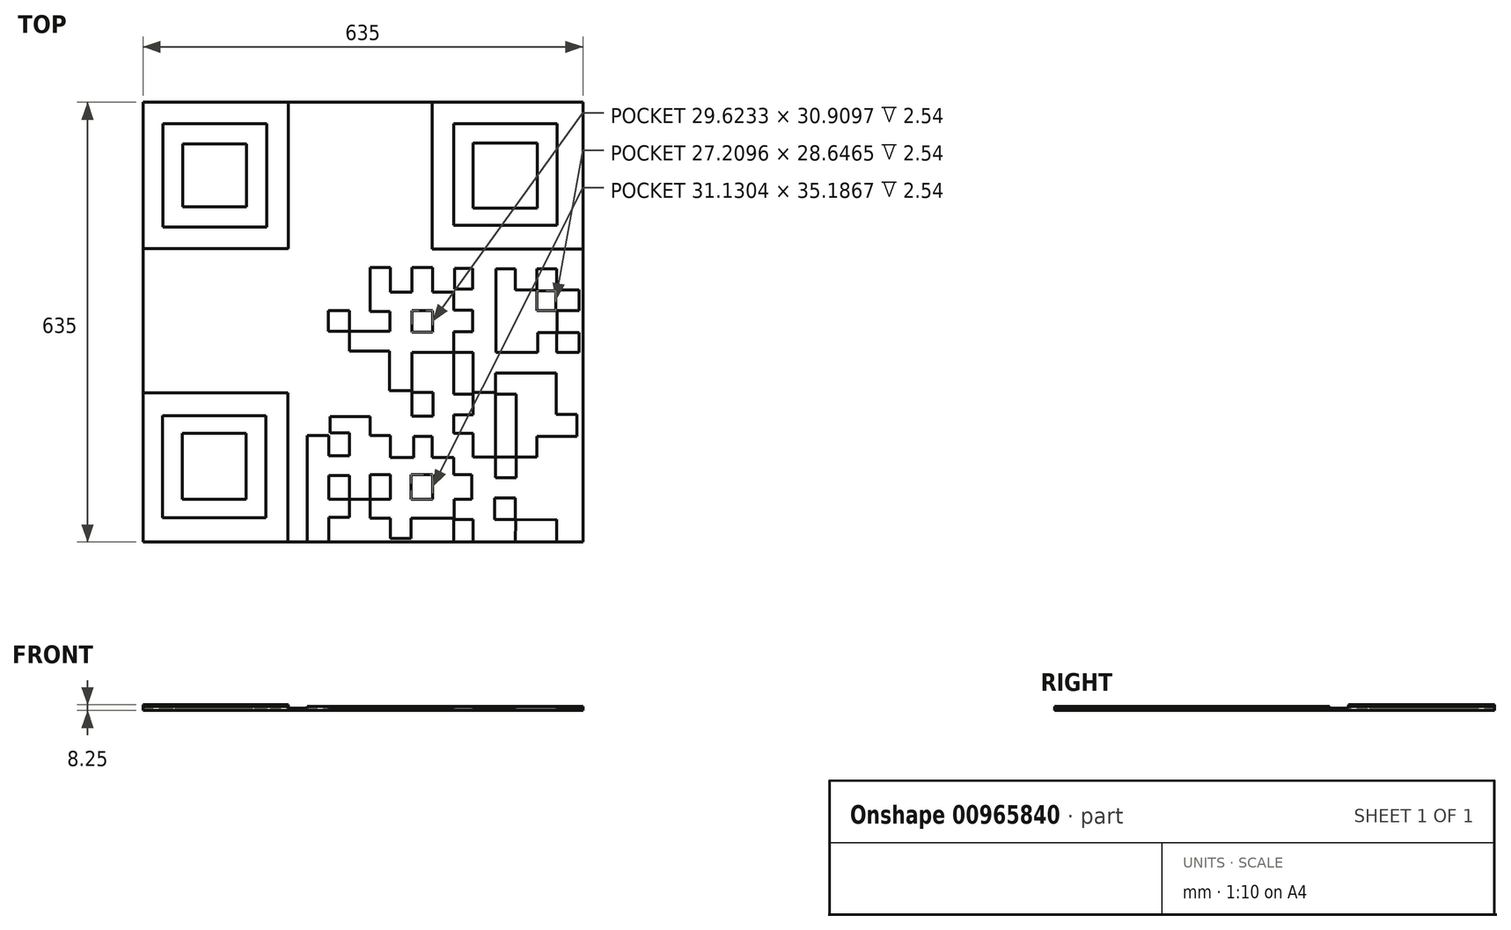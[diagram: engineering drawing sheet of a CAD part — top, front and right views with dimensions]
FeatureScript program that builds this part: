
annotation { "Feature Type Name" : "Feature", "Feature Type Description" : "" }
export const myFeature = defineFeature(function(context is Context, id is Id, definition is map)
    precondition{}
    {
        {
            var Q0;
            Q0=qCreatedBy(makeId("Top.planeOp"),FACE);
            var sketch = newSketch(context, id + "F0", { "sketchPlane" : qUnion([Q0])});
            skLineSegment(sketch, "E0.bottom", {"start": v(-317.5, 317.5) * mm, "end": v(317.5, 317.5) * mm});
            skLineSegment(sketch, "E0.top", {"start": v(-317.5, -317.5) * mm, "end": v(317.5, -317.5) * mm});
            skLineSegment(sketch, "E0.left", {"start": v(-317.5, 317.5) * mm, "end": v(-317.5, -317.5) * mm});
            skLineSegment(sketch, "E0.right", {"start": v(317.5, 317.5) * mm, "end": v(317.5, -317.5) * mm});
            skPoint(sketch, "E0.middle", {"position": v(0, 0) * mm});
            skSolve(sketch);
        }
        {
            var Q0;
            Q0=makeQuery(id+"F0.imprint","IMPRINT",FACE,{"disambiguationData":[TD([[makeQuery(id+"F0.imprint","IMPRINT",EDGE,{"derivedFrom":sQuery(id+"F0.wireOp",EDGE,"E0.bottom")}),-1.0]])]});
            extrude(context, id + "F1", {"entities" : qUnion([Q0]), "oppositeDirection" : true, "depth" : 3.17 * mm, "offsetDistance" : 25.4 * mm});
        }
        {
            var Q0;
            Q0=makeQuery(id+"F1.opExtrude","CAP_FACE",FACE,{"disambiguationData":[OSD([sQuery(id+"F0.wireOp",EDGE,"E0.bottom"),sQuery(id+"F0.wireOp",EDGE,"E0.top"),sQuery(id+"F0.wireOp",EDGE,"E0.left"),sQuery(id+"F0.wireOp",EDGE,"E0.right")])],"isStart":true});
            var sketch = newSketch(context, id + "F2", { "sketchPlane" : qUnion([Q0])});
            skLineSegment(sketch, "E1.bottom", {"start": v(-317.5, 317.5) * mm, "end": v(-107.8, 317.5) * mm});
            skLineSegment(sketch, "E1.top", {"start": v(-317.5, 106.2) * mm, "end": v(-107.8, 106.2) * mm});
            skLineSegment(sketch, "E1.left", {"start": v(-317.5, 317.5) * mm, "end": v(-317.5, 106.2) * mm});
            skLineSegment(sketch, "E1.right", {"start": v(-107.8, 317.5) * mm, "end": v(-107.8, 106.2) * mm});
            skLineSegment(sketch, "E2.bottom", {"start": v(-288.97, 286.94) * mm, "end": v(-139.14, 286.94) * mm});
            skLineSegment(sketch, "E2.top", {"start": v(-288.97, 137.11) * mm, "end": v(-139.14, 137.11) * mm});
            skLineSegment(sketch, "E2.left", {"start": v(-288.97, 286.94) * mm, "end": v(-288.97, 137.11) * mm});
            skLineSegment(sketch, "E2.right", {"start": v(-139.14, 286.94) * mm, "end": v(-139.14, 137.11) * mm});
            skLineSegment(sketch, "E3.bottom", {"start": v(-168.34, 166.3) * mm, "end": v(-260.2, 166.3) * mm});
            skLineSegment(sketch, "E3.top", {"start": v(-168.34, 257.32) * mm, "end": v(-260.2, 257.32) * mm});
            skLineSegment(sketch, "E3.left", {"start": v(-168.34, 166.3) * mm, "end": v(-168.34, 257.32) * mm});
            skLineSegment(sketch, "E3.right", {"start": v(-260.2, 166.3) * mm, "end": v(-260.2, 257.32) * mm});
            skLineSegment(sketch, "E4.bottom", {"start": v(-78.87, 287.97) * mm, "end": v(-18.76, 287.97) * mm});
            skLineSegment(sketch, "E4.top", {"start": v(-78.87, 257.32) * mm, "end": v(-19.2, 257.32) * mm});
            skLineSegment(sketch, "E4.left", {"start": v(-78.87, 287.97) * mm, "end": v(-78.87, 257.32) * mm});
            skLineSegment(sketch, "E4.right", {"start": v(8.71, 287.97) * mm, "end": v(8.71, 257.32) * mm});
            skLineSegment(sketch, "E5.bottom", {"start": v(8.71, 257.32) * mm, "end": v(40.9, 257.32) * mm});
            skLineSegment(sketch, "E5.top", {"start": v(-18.99, 226.58) * mm, "end": v(40.9, 226.58) * mm});
            skLineSegment(sketch, "E5.left", {"start": v(-19.2, 257.32) * mm, "end": v(-19.2, 226.58) * mm});
            skLineSegment(sketch, "E5.right", {"start": v(69.67, 257.32) * mm, "end": v(69.67, 226.58) * mm});
            skLineSegment(sketch, "E6.bottom", {"start": v(69.67, 167.76) * mm, "end": v(41.78, 167.76) * mm});
            skLineSegment(sketch, "E6.top", {"start": v(69.67, 312.44) * mm, "end": v(40.9, 312.44) * mm});
            skLineSegment(sketch, "E6.left", {"start": v(69.67, 167.76) * mm, "end": v(69.67, 312.44) * mm});
            skLineSegment(sketch, "E6.right", {"start": v(40.9, 167.76) * mm, "end": v(40.9, 226.58) * mm});
            skLineSegment(sketch, "E7.bottom", {"start": v(40.9, 312.44) * mm, "end": v(-18.76, 312.44) * mm});
            skLineSegment(sketch, "E7.top", {"start": v(40.9, 287.97) * mm, "end": v(8.71, 287.97) * mm});
            skLineSegment(sketch, "E7.right", {"start": v(-18.76, 312.44) * mm, "end": v(-18.76, 287.97) * mm});
            skLineSegment(sketch, "E8.trimOffspring", {"start": v(40.9, 257.32) * mm, "end": v(40.9, 287.97) * mm});
            skLineSegment(sketch, "E9.bottom", {"start": v(-19.2, 226.58) * mm, "end": v(-81.01, 226.58) * mm});
            skLineSegment(sketch, "E9.top", {"start": v(-19.2, 165.19) * mm, "end": v(-49.61, 165.19) * mm});
            skLineSegment(sketch, "E9.left", {"start": v(-19.2, 226.24) * mm, "end": v(-19.2, 165.19) * mm});
            skLineSegment(sketch, "E9.right", {"start": v(-81.01, 226.58) * mm, "end": v(-81.01, 197.82) * mm});
            skLineSegment(sketch, "E10.top", {"start": v(-81.01, 197.82) * mm, "end": v(-49.67, 197.82) * mm});
            skLineSegment(sketch, "E10.right", {"start": v(-49.67, 165.19) * mm, "end": v(-49.67, 197.82) * mm});
            skLineSegment(sketch, "E11.bottom", {"start": v(-49.67, 165.19) * mm, "end": v(-81.44, 165.19) * mm});
            skLineSegment(sketch, "E11.top", {"start": v(-49.67, 106.8) * mm, "end": v(-81.44, 106.8) * mm});
            skLineSegment(sketch, "E11.left", {"start": v(-49.67, 165.14) * mm, "end": v(-49.67, 106.83) * mm});
            skLineSegment(sketch, "E11.right", {"start": v(-81.44, 165.19) * mm, "end": v(-81.44, 106.8) * mm});
            skLineSegment(sketch, "E12.bottom", {"start": v(-49.66, 106.8) * mm, "end": v(-19.2, 106.8) * mm});
            skLineSegment(sketch, "E12.top", {"start": v(-49.6, 77.61) * mm, "end": v(-19.2, 77.61) * mm});
            skLineSegment(sketch, "E12.left", {"start": v(-49.67, 106.8) * mm, "end": v(-49.67, 77.61) * mm});
            skLineSegment(sketch, "E12.right", {"start": v(-19.2, 106.73) * mm, "end": v(-19.2, 77.61) * mm});
            skLineSegment(sketch, "E13.bottom", {"start": v(-19.12, 106.8) * mm, "end": v(11.29, 106.8) * mm});
            skLineSegment(sketch, "E13.top", {"start": v(-19.2, 137.71) * mm, "end": v(11.29, 137.71) * mm});
            skLineSegment(sketch, "E13.left", {"start": v(-19.2, 106.8) * mm, "end": v(-19.2, 137.71) * mm});
            skLineSegment(sketch, "E13.right", {"start": v(11.29, 106.8) * mm, "end": v(11.29, 136.75) * mm});
            skLineSegment(sketch, "E14.top", {"start": v(11.29, 167.76) * mm, "end": v(40.9, 167.76) * mm});
            skLineSegment(sketch, "E14.left", {"start": v(11.29, 137.71) * mm, "end": v(11.29, 167.76) * mm});
            skLineSegment(sketch, "E15.bottom", {"start": v(41.78, 137.71) * mm, "end": v(71.39, 137.71) * mm});
            skLineSegment(sketch, "E15.top", {"start": v(40.9, 106.8) * mm, "end": v(71.39, 106.8) * mm});
            skLineSegment(sketch, "E15.left", {"start": v(40.9, 136.75) * mm, "end": v(40.9, 106.8) * mm});
            skLineSegment(sketch, "E15.right", {"start": v(71.39, 137.71) * mm, "end": v(71.39, 106.8) * mm});
            skLineSegment(sketch, "E16.bottom", {"start": v(-49.67, 77.61) * mm, "end": v(-139.83, 77.61) * mm});
            skLineSegment(sketch, "E16.top", {"start": v(-49.67, 18.37) * mm, "end": v(-79.72, 18.37) * mm});
            skLineSegment(sketch, "E16.left", {"start": v(-49.67, 77.5) * mm, "end": v(-49.67, 18.37) * mm});
            skLineSegment(sketch, "E16.right", {"start": v(-139.83, 77.61) * mm, "end": v(-139.83, 46.45) * mm});
            skLineSegment(sketch, "E17.top", {"start": v(-139.83, 45.84) * mm, "end": v(-79.72, 45.84) * mm});
            skLineSegment(sketch, "E17.right", {"start": v(-79.72, 18.37) * mm, "end": v(-79.72, 45.84) * mm});
            skLineSegment(sketch, "E18.top", {"start": v(-49.67, -13.4) * mm, "end": v(-19.57, -13.4) * mm});
            skLineSegment(sketch, "E18.left", {"start": v(-49.67, 16.72) * mm, "end": v(-49.67, -13.4) * mm});
            skLineSegment(sketch, "E18.right", {"start": v(-19.2, 16.72) * mm, "end": v(-19.2, -13.02) * mm});
            skLineSegment(sketch, "E19.bottom", {"start": v(-168.57, 77.61) * mm, "end": v(-317.5, 77.61) * mm});
            skLineSegment(sketch, "E19.top", {"start": v(-141.83, 16.72) * mm, "end": v(-168.57, 16.72) * mm});
            skLineSegment(sketch, "E19.right", {"start": v(-317.5, 77.61) * mm, "end": v(-317.5, 16.72) * mm});
            skLineSegment(sketch, "E20.top", {"start": v(-168.58, 46.45) * mm, "end": v(-201.07, 46.45) * mm});
            skLineSegment(sketch, "E20.left", {"start": v(-168.57, 16.72) * mm, "end": v(-168.57, 46.45) * mm});
            skLineSegment(sketch, "E20.right", {"start": v(-201.07, 16.72) * mm, "end": v(-201.07, 46.45) * mm});
            skLineSegment(sketch, "E21.bottom", {"start": v(-168.57, 46.45) * mm, "end": v(-139.83, 46.45) * mm});
            skLineSegment(sketch, "E21.left", {"start": v(-168.57, 46.45) * mm, "end": v(-168.57, 77.61) * mm});
            skLineSegment(sketch, "E21.right", {"start": v(-139.83, 46.45) * mm, "end": v(-139.83, 77.61) * mm});
            skLineSegment(sketch, "E22.trimOffspring", {"start": v(-201.07, 16.72) * mm, "end": v(-287.35, 16.72) * mm});
            skLineSegment(sketch, "E23.bottom", {"start": v(-287.35, 16.72) * mm, "end": v(-200.93, 16.72) * mm});
            skLineSegment(sketch, "E23.top", {"start": v(-317.5, -74.55) * mm, "end": v(-260.39, -74.55) * mm});
            skLineSegment(sketch, "E23.left", {"start": v(-317.5, 16.72) * mm, "end": v(-317.5, -74.55) * mm});
            skLineSegment(sketch, "E23.right", {"start": v(-200.93, -13.7) * mm, "end": v(-200.93, -74.55) * mm});
            skLineSegment(sketch, "E24.top", {"start": v(-227.2, -43.44) * mm, "end": v(-260.39, -43.44) * mm});
            skLineSegment(sketch, "E24.left", {"start": v(-227.2, -74.55) * mm, "end": v(-227.2, -43.44) * mm});
            skLineSegment(sketch, "E24.right", {"start": v(-260.39, -74.55) * mm, "end": v(-260.39, -43.44) * mm});
            skLineSegment(sketch, "E25.bottom", {"start": v(-200.93, 16.72) * mm, "end": v(-287.35, 16.72) * mm});
            skLineSegment(sketch, "E25.top", {"start": v(-200.93, -13.7) * mm, "end": v(-287.35, -13.7) * mm});
            skLineSegment(sketch, "E25.right", {"start": v(-287.35, 16.72) * mm, "end": v(-287.35, -13.7) * mm});
            skLineSegment(sketch, "E26.trimOffspring", {"start": v(-227.2, -74.55) * mm, "end": v(-200.93, -74.55) * mm});
            skLineSegment(sketch, "E27.bottom", {"start": v(-317.5, -102.04) * mm, "end": v(-108.21, -102.04) * mm});
            skLineSegment(sketch, "E27.top", {"start": v(-317.5, -317.5) * mm, "end": v(-108.21, -317.5) * mm});
            skLineSegment(sketch, "E27.left", {"start": v(-317.5, -102.04) * mm, "end": v(-317.5, -317.5) * mm});
            skLineSegment(sketch, "E27.right", {"start": v(-108.21, -102.04) * mm, "end": v(-108.21, -317.5) * mm});
            skLineSegment(sketch, "E28.bottom", {"start": v(-140.2, -282.24) * mm, "end": v(-289.48, -282.24) * mm});
            skLineSegment(sketch, "E28.top", {"start": v(-140.2, -135.1) * mm, "end": v(-289.48, -135.1) * mm});
            skLineSegment(sketch, "E28.left", {"start": v(-140.2, -282.24) * mm, "end": v(-140.2, -135.1) * mm});
            skLineSegment(sketch, "E28.right", {"start": v(-289.48, -282.24) * mm, "end": v(-289.48, -135.1) * mm});
            skLineSegment(sketch, "E29.bottom", {"start": v(-260.69, -160.15) * mm, "end": v(-168.46, -160.15) * mm});
            skLineSegment(sketch, "E29.top", {"start": v(-260.69, -255.58) * mm, "end": v(-168.46, -255.58) * mm});
            skLineSegment(sketch, "E29.left", {"start": v(-260.69, -160.15) * mm, "end": v(-260.69, -255.58) * mm});
            skLineSegment(sketch, "E29.right", {"start": v(-168.46, -160.15) * mm, "end": v(-168.46, -255.58) * mm});
            skLineSegment(sketch, "E30.bottom", {"start": v(-80.5, -163.88) * mm, "end": v(-49.57, -163.88) * mm});
            skLineSegment(sketch, "E30.top", {"start": v(-80.5, -317.5) * mm, "end": v(-49.57, -317.5) * mm});
            skLineSegment(sketch, "E30.left", {"start": v(-80.5, -163.88) * mm, "end": v(-80.5, -317.5) * mm});
            skLineSegment(sketch, "E30.right", {"start": v(-49.57, -163.88) * mm, "end": v(-49.57, -192.67) * mm});
            skLineSegment(sketch, "E31.bottom", {"start": v(-49.57, -281.7) * mm, "end": v(-19.71, -281.7) * mm});
            skLineSegment(sketch, "E31.top", {"start": v(-49.57, -255.58) * mm, "end": v(-19.72, -255.58) * mm});
            skLineSegment(sketch, "E31.right", {"start": v(-19.71, -281.7) * mm, "end": v(-19.71, -255.59) * mm});
            skLineSegment(sketch, "E32.bottom", {"start": v(-19.7, -255.58) * mm, "end": v(10.46, -255.58) * mm});
            skLineSegment(sketch, "E32.top", {"start": v(9.93, -135.18) * mm, "end": v(10.47, -135.18) * mm});
            skLineSegment(sketch, "E32.left", {"start": v(-19.71, -255.58) * mm, "end": v(-19.71, -221.46) * mm});
            skLineSegment(sketch, "E32.right", {"start": v(10.47, -255.57) * mm, "end": v(10.47, -220.4) * mm});
            skLineSegment(sketch, "E33.top", {"start": v(-19.71, -159.62) * mm, "end": v(-47.44, -159.62) * mm});
            skLineSegment(sketch, "E33.right", {"start": v(-47.44, -136.16) * mm, "end": v(-47.44, -159.62) * mm});
            skLineSegment(sketch, "E34.bottom", {"start": v(-49.57, -192.67) * mm, "end": v(-19.71, -192.67) * mm});
            skLineSegment(sketch, "E34.top", {"start": v(-49.57, -221.46) * mm, "end": v(-19.71, -221.46) * mm});
            skLineSegment(sketch, "E35.trimOffspring", {"start": v(-19.71, -192.67) * mm, "end": v(-19.71, -159.62) * mm});
            skLineSegment(sketch, "E36.trimOffspring", {"start": v(-49.57, -221.46) * mm, "end": v(-49.57, -255.58) * mm});
            skLineSegment(sketch, "E37.trimOffspring", {"start": v(-49.57, -281.7) * mm, "end": v(-49.57, -317.5) * mm});
            skLineSegment(sketch, "E38.bottom", {"start": v(10.47, -163.88) * mm, "end": v(39.79, -163.88) * mm});
            skLineSegment(sketch, "E38.top", {"start": v(10.47, -220.4) * mm, "end": v(39.79, -220.4) * mm});
            skLineSegment(sketch, "E38.right", {"start": v(39.79, -163.88) * mm, "end": v(39.79, -195.38) * mm});
            skPoint(sketch, "E39.oppositeSnap0", {"position": v(10.47, -195.38) * mm});
            skLineSegment(sketch, "E39.bottom", {"start": v(69.64, -220.4) * mm, "end": v(100.77, -220.4) * mm});
            skLineSegment(sketch, "E39.top", {"start": v(39.79, -195.38) * mm, "end": v(73.05, -195.38) * mm});
            skLineSegment(sketch, "E39.right", {"start": v(130.95, -220.4) * mm, "end": v(130.95, -195.38) * mm});
            skLineSegment(sketch, "E40.top", {"start": v(99.7, -164.73) * mm, "end": v(73.05, -164.73) * mm});
            skLineSegment(sketch, "E40.left", {"start": v(99.7, -195.38) * mm, "end": v(99.7, -164.73) * mm});
            skLineSegment(sketch, "E40.right", {"start": v(73.05, -195.38) * mm, "end": v(73.05, -164.73) * mm});
            skLineSegment(sketch, "E41.top", {"start": v(39.79, -312.1) * mm, "end": v(69.64, -312.1) * mm});
            skLineSegment(sketch, "E41.left", {"start": v(39.79, -220.4) * mm, "end": v(39.79, -255.58) * mm});
            skLineSegment(sketch, "E41.right", {"start": v(69.64, -220.4) * mm, "end": v(69.64, -255.58) * mm});
            skLineSegment(sketch, "E42.bottom", {"start": v(10.49, -255.58) * mm, "end": v(39.79, -255.58) * mm});
            skLineSegment(sketch, "E42.top", {"start": v(10.47, -282.77) * mm, "end": v(39.79, -282.77) * mm});
            skLineSegment(sketch, "E42.left", {"start": v(10.47, -255.6) * mm, "end": v(10.47, -282.77) * mm});
            skLineSegment(sketch, "E42.right", {"start": v(131.49, -255.58) * mm, "end": v(131.49, -282.77) * mm});
            skLineSegment(sketch, "E43.bottom", {"start": v(157.29, -220.4) * mm, "end": v(130.95, -220.4) * mm});
            skLineSegment(sketch, "E43.top", {"start": v(157.29, -255.58) * mm, "end": v(131.49, -255.58) * mm});
            skLineSegment(sketch, "E43.left", {"start": v(157.29, -220.4) * mm, "end": v(157.29, -255.58) * mm});
            skLineSegment(sketch, "E43.right", {"start": v(100.77, -220.4) * mm, "end": v(100.77, -255.58) * mm});
            skLineSegment(sketch, "E44.top", {"start": v(131.16, -317.5) * mm, "end": v(158.89, -317.5) * mm});
            skLineSegment(sketch, "E44.right", {"start": v(158.89, -284.77) * mm, "end": v(158.89, -317.5) * mm});
            skLineSegment(sketch, "E45.trimOffspring", {"start": v(10.47, -163.88) * mm, "end": v(10.47, -136.16) * mm});
            skLineSegment(sketch, "E46.trimOffspring", {"start": v(39.79, -282.77) * mm, "end": v(39.79, -312.1) * mm});
            skLineSegment(sketch, "E47.trimOffspring", {"start": v(69.64, -282.77) * mm, "end": v(131.49, -282.77) * mm});
            skLineSegment(sketch, "E48.trimOffspring", {"start": v(69.64, -282.77) * mm, "end": v(69.64, -312.1) * mm});
            skLineSegment(sketch, "E49.trimOffspring", {"start": v(69.64, -255.58) * mm, "end": v(100.77, -255.58) * mm});
            skLineSegment(sketch, "E50.trimOffspring", {"start": v(99.7, -195.38) * mm, "end": v(130.95, -195.38) * mm});
            skLineSegment(sketch, "E51.bottom", {"start": v(190.34, -253.98) * mm, "end": v(220.2, -253.98) * mm});
            skLineSegment(sketch, "E51.top", {"start": v(190.34, -284.9) * mm, "end": v(220.2, -284.9) * mm});
            skLineSegment(sketch, "E51.left", {"start": v(190.34, -253.98) * mm, "end": v(190.34, -284.9) * mm});
            skLineSegment(sketch, "E51.right", {"start": v(220.2, -253.98) * mm, "end": v(220.2, -284.9) * mm});
            skLineSegment(sketch, "E52.top", {"start": v(220.2, -317.5) * mm, "end": v(279.37, -317.5) * mm});
            skLineSegment(sketch, "E52.right", {"start": v(279.37, -284.9) * mm, "end": v(279.37, -317.5) * mm});
            skLineSegment(sketch, "E53.bottom", {"start": v(-139.83, 16.72) * mm, "end": v(-80.5, 16.72) * mm});
            skLineSegment(sketch, "E53.top", {"start": v(-139.83, -13.54) * mm, "end": v(-80.5, -13.54) * mm});
            skLineSegment(sketch, "E53.right", {"start": v(-80.5, 16.72) * mm, "end": v(-80.5, -13.54) * mm});
            skLineSegment(sketch, "E54.bottom", {"start": v(-169, -13.54) * mm, "end": v(-141.83, -13.54) * mm});
            skLineSegment(sketch, "E54.top", {"start": v(-169, -75.92) * mm, "end": v(-79.96, -75.92) * mm});
            skLineSegment(sketch, "E54.left", {"start": v(-169, -13.54) * mm, "end": v(-169, -75.92) * mm});
            skLineSegment(sketch, "E54.right", {"start": v(-48.5, -41.26) * mm, "end": v(-48.5, -75.92) * mm});
            skLineSegment(sketch, "E55.bottom", {"start": v(-80.5, -13.54) * mm, "end": v(-139.83, -13.54) * mm});
            skLineSegment(sketch, "E55.top", {"start": v(-48.5, -41.26) * mm, "end": v(-139.83, -41.26) * mm});
            skLineSegment(sketch, "E55.right", {"start": v(-139.83, -13.54) * mm, "end": v(-139.83, -41.26) * mm});
            skLineSegment(sketch, "E56.bottom", {"start": v(-48.5, -75.92) * mm, "end": v(9.93, -75.92) * mm});
            skLineSegment(sketch, "E56.top", {"start": v(-47.44, -136.16) * mm, "end": v(10.47, -136.16) * mm});
            skLineSegment(sketch, "E56.left", {"start": v(-79.96, -75.92) * mm, "end": v(-79.96, -134.56) * mm});
            skLineSegment(sketch, "E56.right", {"start": v(39.79, -104.8) * mm, "end": v(39.79, -135.18) * mm});
            skLineSegment(sketch, "E57.top", {"start": v(-47.44, -104.8) * mm, "end": v(9.55, -104.8) * mm});
            skLineSegment(sketch, "E57.left", {"start": v(-47.44, -134.56) * mm, "end": v(-47.44, -104.8) * mm});
            skLineSegment(sketch, "E57.right", {"start": v(9.93, -135.18) * mm, "end": v(9.93, -105.17) * mm});
            skLineSegment(sketch, "E58.bottom", {"start": v(10.31, -104.8) * mm, "end": v(39.79, -104.8) * mm});
            skLineSegment(sketch, "E58.left", {"start": v(9.93, -104.4) * mm, "end": v(9.93, -75.92) * mm});
            skLineSegment(sketch, "E59.bottom", {"start": v(317.5, 317.5) * mm, "end": v(100.13, 317.5) * mm});
            skLineSegment(sketch, "E59.top", {"start": v(317.5, 105.52) * mm, "end": v(100.13, 105.52) * mm});
            skLineSegment(sketch, "E59.left", {"start": v(317.5, 317.5) * mm, "end": v(317.5, 105.52) * mm});
            skLineSegment(sketch, "E59.right", {"start": v(100.13, 317.5) * mm, "end": v(100.13, 105.52) * mm});
            skLineSegment(sketch, "E60.bottom", {"start": v(131.05, 140.17) * mm, "end": v(280.32, 140.17) * mm});
            skLineSegment(sketch, "E60.top", {"start": v(131.05, 286.79) * mm, "end": v(280.32, 286.79) * mm});
            skLineSegment(sketch, "E60.left", {"start": v(131.05, 140.17) * mm, "end": v(131.05, 286.79) * mm});
            skLineSegment(sketch, "E60.right", {"start": v(280.32, 140.17) * mm, "end": v(280.32, 286.79) * mm});
            skLineSegment(sketch, "E61.bottom", {"start": v(251.53, 258.53) * mm, "end": v(158.77, 258.53) * mm});
            skLineSegment(sketch, "E61.top", {"start": v(251.53, 164.7) * mm, "end": v(158.77, 164.7) * mm});
            skLineSegment(sketch, "E61.left", {"start": v(251.53, 258.53) * mm, "end": v(251.53, 164.7) * mm});
            skLineSegment(sketch, "E61.right", {"start": v(158.77, 258.53) * mm, "end": v(158.77, 164.7) * mm});
            skLineSegment(sketch, "E62.bottom", {"start": v(10.53, 78.94) * mm, "end": v(39.67, 78.94) * mm});
            skLineSegment(sketch, "E62.left", {"start": v(10.53, 78.94) * mm, "end": v(10.53, 15.38) * mm});
            skLineSegment(sketch, "E62.right", {"start": v(70.78, 16.58) * mm, "end": v(70.78, -14.33) * mm});
            skLineSegment(sketch, "E63.right", {"start": v(38.34, -98.9) * mm, "end": v(38.34, -45.53) * mm});
            skLineSegment(sketch, "E64.top", {"start": v(10.53, 15.38) * mm, "end": v(39, 15.38) * mm});
            skLineSegment(sketch, "E64.right", {"start": v(39, -11.1) * mm, "end": v(39, 15.38) * mm});
            skLineSegment(sketch, "E65.top", {"start": v(70.78, 43.19) * mm, "end": v(39.67, 43.19) * mm});
            skLineSegment(sketch, "E65.left", {"start": v(70.78, 78.94) * mm, "end": v(70.78, 43.19) * mm});
            skLineSegment(sketch, "E65.right", {"start": v(39.67, 78.94) * mm, "end": v(39.67, 43.19) * mm});
            skLineSegment(sketch, "E66.bottom", {"start": v(70.78, 78.94) * mm, "end": v(100.4, 78.94) * mm});
            skLineSegment(sketch, "E66.top", {"start": v(70.78, 16.58) * mm, "end": v(100.4, 16.58) * mm});
            skLineSegment(sketch, "E66.right", {"start": v(100.4, 78.94) * mm, "end": v(100.4, 43.19) * mm});
            skPoint(sketch, "E67.firstSnap0", {"position": v(100.4, 47.76) * mm});
            skLineSegment(sketch, "E67.bottom", {"start": v(100.4, 43.19) * mm, "end": v(131.32, 43.19) * mm});
            skLineSegment(sketch, "E67.top", {"start": v(100.4, -43.44) * mm, "end": v(130.93, -43.44) * mm});
            skLineSegment(sketch, "E67.left", {"start": v(100.4, 16.58) * mm, "end": v(100.4, -14.33) * mm});
            skLineSegment(sketch, "E67.right", {"start": v(131.32, 43.19) * mm, "end": v(131.32, 17.17) * mm});
            skLineSegment(sketch, "E68.bottom", {"start": v(100.4, -43.44) * mm, "end": v(70.78, -43.44) * mm});
            skLineSegment(sketch, "E68.top", {"start": v(100.4, -14.33) * mm, "end": v(70.78, -14.33) * mm});
            skLineSegment(sketch, "E69.trimOffspring", {"start": v(70.78, -43.44) * mm, "end": v(70.78, -98.9) * mm});
            skLineSegment(sketch, "E70.bottom", {"start": v(-18.97, -13.4) * mm, "end": v(10.53, -13.4) * mm});
            skLineSegment(sketch, "E70.top", {"start": v(-19.2, -41.38) * mm, "end": v(10.53, -41.38) * mm});
            skLineSegment(sketch, "E70.left", {"start": v(-19.2, -13.67) * mm, "end": v(-19.2, -41.38) * mm});
            skLineSegment(sketch, "E71", {"start": v(10.53, -13.4) * mm, "end": v(14.68, -13.4) * mm});
            skLineSegment(sketch, "E72", {"start": v(39, -11.1) * mm, "end": v(39, -13.4) * mm});
            skLineSegment(sketch, "E73", {"start": v(39, -13.4) * mm, "end": v(14.68, -13.4) * mm});
            skLineSegment(sketch, "E74", {"start": v(10.53, -41.38) * mm, "end": v(38.34, -41.38) * mm});
            skLineSegment(sketch, "E75", {"start": v(38.34, -41.38) * mm, "end": v(38.34, -45.53) * mm});
            skPoint(sketch, "E76.orphan", {"position": v(10.53, -11.1) * mm});
            skLineSegment(sketch, "E77.bottom", {"start": v(132.14, 47.85) * mm, "end": v(158.41, 47.85) * mm});
            skLineSegment(sketch, "E77.top", {"start": v(132.14, 77.93) * mm, "end": v(158.41, 77.93) * mm});
            skLineSegment(sketch, "E77.left", {"start": v(132.14, 47.85) * mm, "end": v(132.14, 77.93) * mm});
            skLineSegment(sketch, "E77.right", {"start": v(158.41, 47.85) * mm, "end": v(158.41, 77.93) * mm});
            skLineSegment(sketch, "E78.bottom", {"start": v(131.32, 17.17) * mm, "end": v(158.35, 17.17) * mm});
            skLineSegment(sketch, "E78.top", {"start": v(131.32, -13.6) * mm, "end": v(158.35, -13.6) * mm});
            skLineSegment(sketch, "E78.right", {"start": v(158.35, 17.17) * mm, "end": v(158.35, -13.6) * mm});
            skLineSegment(sketch, "E79.bottom", {"start": v(192.29, 76.9) * mm, "end": v(219.94, 76.9) * mm});
            skLineSegment(sketch, "E79.top", {"start": v(192.29, -43.4) * mm, "end": v(252.1, -43.4) * mm});
            skLineSegment(sketch, "E79.left", {"start": v(192.29, 76.9) * mm, "end": v(192.29, -43.4) * mm});
            skLineSegment(sketch, "E79.right", {"start": v(311.9, 46.47) * mm, "end": v(311.9, 16.74) * mm});
            skLineSegment(sketch, "E80.top", {"start": v(219.94, 46.47) * mm, "end": v(251.06, 46.47) * mm});
            skLineSegment(sketch, "E80.left", {"start": v(219.94, 76.9) * mm, "end": v(219.94, 46.47) * mm});
            skLineSegment(sketch, "E80.right", {"start": v(251.06, 76.9) * mm, "end": v(251.06, 46.47) * mm});
            skLineSegment(sketch, "E81.top", {"start": v(251.06, 16.74) * mm, "end": v(278.27, 16.74) * mm});
            skLineSegment(sketch, "E81.left", {"start": v(251.06, 45.39) * mm, "end": v(251.06, 16.74) * mm});
            skLineSegment(sketch, "E82.bottom", {"start": v(279.97, 16.74) * mm, "end": v(311.9, 16.74) * mm});
            skLineSegment(sketch, "E82.top", {"start": v(279.97, -15.06) * mm, "end": v(311.9, -15.06) * mm});
            skLineSegment(sketch, "E83.bottom", {"start": v(279.4, -15.06) * mm, "end": v(252.1, -15.06) * mm});
            skLineSegment(sketch, "E83.left", {"start": v(279.4, -15.06) * mm, "end": v(279.4, -43.4) * mm});
            skLineSegment(sketch, "E83.right", {"start": v(252.1, -15.06) * mm, "end": v(252.1, -43.4) * mm});
            skLineSegment(sketch, "E84.bottom", {"start": v(279.4, 46.47) * mm, "end": v(311.9, 46.47) * mm});
            skLineSegment(sketch, "E84.left", {"start": v(279.4, 46.47) * mm, "end": v(279.4, 76.9) * mm});
            skLineSegment(sketch, "E85.trimOffspring", {"start": v(311.9, -15.06) * mm, "end": v(311.9, -43.4) * mm});
            skLineSegment(sketch, "E86.trimOffspring", {"start": v(251.06, 76.9) * mm, "end": v(279.4, 76.9) * mm});
            skLineSegment(sketch, "E87.trimOffspring", {"start": v(279.4, -43.4) * mm, "end": v(311.9, -43.4) * mm});
            skLineSegment(sketch, "E88.bottom", {"start": v(131.7, -43.44) * mm, "end": v(159.16, -43.44) * mm});
            skLineSegment(sketch, "E88.top", {"start": v(131.32, -103.81) * mm, "end": v(159.16, -103.81) * mm});
            skLineSegment(sketch, "E88.left", {"start": v(131.32, -43.82) * mm, "end": v(131.32, -103.81) * mm});
            skLineSegment(sketch, "E88.right", {"start": v(159.16, -43.44) * mm, "end": v(159.16, -101.55) * mm});
            skLineSegment(sketch, "E89.top", {"start": v(159.16, -194.55) * mm, "end": v(190.76, -194.55) * mm});
            skLineSegment(sketch, "E89.left", {"start": v(159.16, -103.81) * mm, "end": v(159.16, -133.67) * mm});
            skLineSegment(sketch, "E89.right", {"start": v(191.14, -103.81) * mm, "end": v(191.14, -194.17) * mm});
            skLineSegment(sketch, "E90.bottom", {"start": v(191.53, -194.55) * mm, "end": v(220.62, -194.55) * mm});
            skLineSegment(sketch, "E90.top", {"start": v(191.14, -224.4) * mm, "end": v(221, -224.4) * mm});
            skLineSegment(sketch, "E90.left", {"start": v(191.14, -194.93) * mm, "end": v(191.14, -224.4) * mm});
            skLineSegment(sketch, "E90.right", {"start": v(221, -194.93) * mm, "end": v(221, -224.4) * mm});
            skLineSegment(sketch, "E91.bottom", {"start": v(221.38, -194.55) * mm, "end": v(250.85, -194.55) * mm});
            skLineSegment(sketch, "E91.top", {"start": v(221, -73.42) * mm, "end": v(250.85, -73.42) * mm});
            skLineSegment(sketch, "E91.left", {"start": v(221, -194.17) * mm, "end": v(221, -103.81) * mm});
            skLineSegment(sketch, "E91.right", {"start": v(250.85, -194.55) * mm, "end": v(250.85, -164.7) * mm});
            skLineSegment(sketch, "E92.bottom", {"start": v(250.85, -73.42) * mm, "end": v(279.11, -73.42) * mm});
            skLineSegment(sketch, "E92.top", {"start": v(250.85, -164.7) * mm, "end": v(279.11, -164.7) * mm});
            skLineSegment(sketch, "E92.right", {"start": v(279.11, -73.42) * mm, "end": v(279.11, -133.24) * mm});
            skLineSegment(sketch, "E93.bottom", {"start": v(279.11, -164.7) * mm, "end": v(308.97, -164.7) * mm});
            skLineSegment(sketch, "E93.top", {"start": v(279.11, -133.24) * mm, "end": v(308.97, -133.24) * mm});
            skLineSegment(sketch, "E93.right", {"start": v(308.97, -164.7) * mm, "end": v(308.97, -133.24) * mm});
            skLineSegment(sketch, "E94.bottom", {"start": v(221, -73.42) * mm, "end": v(191.14, -73.42) * mm});
            skLineSegment(sketch, "E94.top", {"start": v(221, -103.81) * mm, "end": v(191.14, -103.81) * mm});
            skLineSegment(sketch, "E94.right", {"start": v(191.14, -73.42) * mm, "end": v(191.14, -101.55) * mm});
            skLineSegment(sketch, "E95.bottom", {"start": v(159.16, -133.67) * mm, "end": v(131.32, -133.67) * mm});
            skLineSegment(sketch, "E95.top", {"start": v(159.16, -160.32) * mm, "end": v(131.32, -160.32) * mm});
            skLineSegment(sketch, "E95.right", {"start": v(131.32, -133.67) * mm, "end": v(131.32, -160.32) * mm});
            skLineSegment(sketch, "E96.bottom", {"start": v(70.78, -101.14) * mm, "end": v(101.39, -101.14) * mm});
            skLineSegment(sketch, "E96.top", {"start": v(70.78, -135.89) * mm, "end": v(101.39, -135.89) * mm});
            skLineSegment(sketch, "E96.left", {"start": v(70.78, -101.14) * mm, "end": v(70.78, -135.89) * mm});
            skLineSegment(sketch, "E96.right", {"start": v(101.39, -101.14) * mm, "end": v(101.39, -135.89) * mm});
            skLineSegment(sketch, "E97.trimOffspring", {"start": v(159.16, -160.32) * mm, "end": v(159.16, -194.55) * mm});
            skLineSegment(sketch, "E98.trimOffspring", {"start": v(131.32, -13.6) * mm, "end": v(131.32, -43.06) * mm});
            skLineSegment(sketch, "E99", {"start": v(10.47, -135.18) * mm, "end": v(39.79, -135.18) * mm});
            skLineSegment(sketch, "E100", {"start": v(158.89, -284.77) * mm, "end": v(131.16, -284.77) * mm});
            skLineSegment(sketch, "E101", {"start": v(131.16, -284.77) * mm, "end": v(131.16, -317.5) * mm});
            skLineSegment(sketch, "E102", {"start": v(220.2, -317.5) * mm, "end": v(220.3, -285.44) * mm});
            skLineSegment(sketch, "E103", {"start": v(220.3, -285.44) * mm, "end": v(279.37, -284.9) * mm});
            skLineSegment(sketch, "E104.bottom", {"start": v(221, -194.17) * mm, "end": v(220.62, -194.17) * mm});
            skLineSegment(sketch, "E104.top", {"start": v(221.38, -194.93) * mm, "end": v(221, -194.93) * mm});
            skLineSegment(sketch, "E104.left", {"start": v(221.38, -194.55) * mm, "end": v(221.38, -194.93) * mm});
            skLineSegment(sketch, "E104.right", {"start": v(220.62, -194.17) * mm, "end": v(220.62, -194.55) * mm});
            skPoint(sketch, "E104.middle", {"position": v(221, -194.55) * mm});
            skPoint(sketch, "E105.orphan", {"position": v(221.38, -194.17) * mm});
            skPoint(sketch, "E106.orphan", {"position": v(220.62, -194.93) * mm});
            skLineSegment(sketch, "E107.trimOffspring", {"start": v(-139.83, 45.84) * mm, "end": v(-139.83, 16.72) * mm});
            skPoint(sketch, "E108.orphan", {"position": v(10.53, -101.14) * mm});
            skLineSegment(sketch, "E109", {"start": v(38.34, -98.9) * mm, "end": v(70.78, -98.9) * mm});
            skLineSegment(sketch, "E110.bottom", {"start": v(9.93, -104.4) * mm, "end": v(10.31, -104.4) * mm});
            skLineSegment(sketch, "E110.top", {"start": v(9.55, -105.17) * mm, "end": v(9.93, -105.17) * mm});
            skLineSegment(sketch, "E110.left", {"start": v(9.55, -104.8) * mm, "end": v(9.55, -105.17) * mm});
            skLineSegment(sketch, "E110.right", {"start": v(10.31, -104.4) * mm, "end": v(10.31, -104.8) * mm});
            skPoint(sketch, "E110.middle", {"position": v(9.93, -104.8) * mm});
            skLineSegment(sketch, "E111", {"start": v(-47.44, -134.56) * mm, "end": v(-79.96, -134.56) * mm});
            skPoint(sketch, "E112.orphan", {"position": v(9.55, -104.4) * mm});
            skPoint(sketch, "E113.orphan", {"position": v(10.31, -105.17) * mm});
            skLineSegment(sketch, "E114.bottom", {"start": v(131.32, -43.06) * mm, "end": v(131.7, -43.06) * mm});
            skLineSegment(sketch, "E114.top", {"start": v(130.93, -43.82) * mm, "end": v(131.32, -43.82) * mm});
            skLineSegment(sketch, "E114.left", {"start": v(130.93, -43.44) * mm, "end": v(130.93, -43.82) * mm});
            skLineSegment(sketch, "E114.right", {"start": v(131.7, -43.06) * mm, "end": v(131.7, -43.44) * mm});
            skPoint(sketch, "E114.middle", {"position": v(131.32, -43.44) * mm});
            skPoint(sketch, "E115.orphan", {"position": v(131.7, -43.82) * mm});
            skPoint(sketch, "E116.orphan", {"position": v(130.93, -43.06) * mm});
            skLineSegment(sketch, "E117", {"start": v(159.16, -101.55) * mm, "end": v(191.14, -101.55) * mm});
            skLineSegment(sketch, "E118.bottom", {"start": v(191.14, -194.17) * mm, "end": v(191.53, -194.17) * mm});
            skLineSegment(sketch, "E118.top", {"start": v(190.76, -194.93) * mm, "end": v(191.14, -194.93) * mm});
            skLineSegment(sketch, "E118.left", {"start": v(190.76, -194.55) * mm, "end": v(190.76, -194.93) * mm});
            skLineSegment(sketch, "E118.right", {"start": v(191.53, -194.17) * mm, "end": v(191.53, -194.55) * mm});
            skPoint(sketch, "E118.middle", {"position": v(191.14, -194.55) * mm});
            skPoint(sketch, "E119.orphan", {"position": v(190.76, -194.17) * mm});
            skPoint(sketch, "E120.orphan", {"position": v(191.53, -194.93) * mm});
            skLineSegment(sketch, "E121", {"start": v(-19.2, -13.02) * mm, "end": v(-18.97, -13.4) * mm});
            skLineSegment(sketch, "E122", {"start": v(-19.57, -13.4) * mm, "end": v(-19.2, -13.67) * mm});
            skPoint(sketch, "E123.orphan", {"position": v(-19.2, -13.4) * mm});
            skLineSegment(sketch, "E124", {"start": v(-141.83, 16.72) * mm, "end": v(-141.83, -13.54) * mm});
            skLineSegment(sketch, "E125", {"start": v(-168.58, 46.45) * mm, "end": v(-168.57, 46.45) * mm});
            skLineSegment(sketch, "E126", {"start": v(-49.67, 16.72) * mm, "end": v(-19.2, 16.72) * mm});
            skLineSegment(sketch, "E127", {"start": v(41.78, 167.76) * mm, "end": v(41.78, 137.71) * mm});
            skLineSegment(sketch, "E128", {"start": v(40.9, 136.75) * mm, "end": v(11.29, 136.75) * mm});
            skLineSegment(sketch, "E129", {"start": v(-49.6, 77.61) * mm, "end": v(-49.67, 77.5) * mm});
            skLineSegment(sketch, "E130", {"start": v(-19.12, 106.8) * mm, "end": v(-19.2, 106.73) * mm});
            skLineSegment(sketch, "E131", {"start": v(-49.67, 106.83) * mm, "end": v(-49.66, 106.8) * mm});
            skLineSegment(sketch, "E132", {"start": v(-19.2, 226.24) * mm, "end": v(-18.99, 226.58) * mm});
            skLineSegment(sketch, "E133", {"start": v(-49.67, 165.14) * mm, "end": v(-49.61, 165.19) * mm});
            skLineSegment(sketch, "E134", {"start": v(279.97, 16.74) * mm, "end": v(279.97, -15.06) * mm});
            skLineSegment(sketch, "E135", {"start": v(278.27, 16.74) * mm, "end": v(278.27, 45.39) * mm});
            skLineSegment(sketch, "E136", {"start": v(278.27, 45.39) * mm, "end": v(251.06, 45.39) * mm});
            skLineSegment(sketch, "E137", {"start": v(10.47, -255.6) * mm, "end": v(10.49, -255.58) * mm});
            skLineSegment(sketch, "E138", {"start": v(10.46, -255.58) * mm, "end": v(10.47, -255.57) * mm});
            skPoint(sketch, "E139.orphan", {"position": v(10.47, -255.58) * mm});
            skLineSegment(sketch, "E140", {"start": v(-19.72, -255.58) * mm, "end": v(-19.71, -255.59) * mm});
            skLineSegment(sketch, "E141", {"start": v(-19.71, -255.58) * mm, "end": v(-19.7, -255.58) * mm});
            skSolve(sketch);
        }
        {
            var Q0;
            Q0=makeQuery(id+"F2.imprint","IMPRINT",FACE,{"disambiguationData":[TD([[makeQuery(id+"F2.imprint","IMPRINT",EDGE,{"derivedFrom":sQuery(id+"F2.wireOp",EDGE,"E1.bottom")}),-1.0]])]});
            extrude(context, id + "F3", {"entities" : qUnion([Q0]), "operationType" : NewBodyOperationType.ADD, "depth" : 2.54 * mm, "offsetDistance" : 25.4 * mm});
        }
        {
            var Q0;
            Q0=makeQuery(id+"F2.imprint","IMPRINT",FACE,{"disambiguationData":[TD([[makeQuery(id+"F2.imprint","IMPRINT",EDGE,{"derivedFrom":sQuery(id+"F2.wireOp",EDGE,"E16.bottom")}),1.0]])]});
            var Q1;
            Q1=makeQuery(id+"F2.imprint","IMPRINT",FACE,{"disambiguationData":[TD([[makeQuery(id+"F2.imprint","IMPRINT",EDGE,{"derivedFrom":sQuery(id+"F2.wireOp",EDGE,"E59.bottom")}),-1.0]])]});
            var Q2;
            Q2=makeQuery(id+"F2.imprint","IMPRINT",FACE,{"disambiguationData":[TD([[makeQuery(id+"F2.imprint","IMPRINT",EDGE,{"derivedFrom":sQuery(id+"F2.wireOp",EDGE,"E61.bottom")}),1.0]])]});
            var Q3;
            Q3=makeQuery(id+"F2.imprint","IMPRINT",FACE,{"disambiguationData":[TD([[makeQuery(id+"F2.imprint","IMPRINT",EDGE,{"derivedFrom":sQuery(id+"F2.wireOp",EDGE,"E3.bottom")}),-1.0]])]});
            var Q4;
            Q4=makeQuery(id+"F3.opExtrude","CAP_FACE",FACE,{"disambiguationData":[OSD([sQuery(id+"F2.wireOp",EDGE,"E1.bottom"),sQuery(id+"F2.wireOp",EDGE,"E1.top"),sQuery(id+"F2.wireOp",EDGE,"E1.left"),sQuery(id+"F2.wireOp",EDGE,"E1.right"),sQuery(id+"F2.wireOp",EDGE,"E2.bottom"),sQuery(id+"F2.wireOp",EDGE,"E2.top"),sQuery(id+"F2.wireOp",EDGE,"E2.left"),sQuery(id+"F2.wireOp",EDGE,"E2.right")])],"isStart":false});
            var Q5;
            Q5=makeQuery(id+"F2.imprint","IMPRINT",FACE,{"disambiguationData":[TD([[makeQuery(id+"F2.imprint","IMPRINT",EDGE,{"derivedFrom":sQuery(id+"F2.wireOp",EDGE,"E29.bottom")}),-1.0]])]});
            var Q6;
            Q6=makeQuery(id+"F2.imprint","IMPRINT",FACE,{"disambiguationData":[TD([[makeQuery(id+"F2.imprint","IMPRINT",EDGE,{"derivedFrom":sQuery(id+"F2.wireOp",EDGE,"E27.bottom")}),-1.0]])]});
            var Q7;
            Q7=makeQuery(id+"F2.imprint","IMPRINT",FACE,{"disambiguationData":[TD([[makeQuery(id+"F2.imprint","IMPRINT",EDGE,{"derivedFrom":sQuery(id+"F2.wireOp",EDGE,"E44.top")}),1.0]])]});
            var Q8;
            Q8=makeQuery(id+"F2.imprint","IMPRINT",FACE,{"disambiguationData":[TD([[makeQuery(id+"F2.imprint","IMPRINT",EDGE,{"derivedFrom":sQuery(id+"F2.wireOp",EDGE,"E52.top")}),1.0]])]});
            var Q9;
            Q9=makeQuery(id+"F2.imprint","IMPRINT",FACE,{"disambiguationData":[TD([[makeQuery(id+"F2.imprint","IMPRINT",EDGE,{"derivedFrom":sQuery(id+"F2.wireOp",EDGE,"E51.bottom")}),-1.0]])]});
            var Q10;
            Q10=makeQuery(id+"F2.imprint","IMPRINT",FACE,{"disambiguationData":[TD([[makeQuery(id+"F2.imprint","IMPRINT",EDGE,{"derivedFrom":sQuery(id+"F2.wireOp",EDGE,"E79.bottom")}),-1.0]])]});
            var Q11;
            Q11=makeQuery(id+"F2.imprint","IMPRINT",FACE,{"disambiguationData":[TD([[makeQuery(id+"F2.imprint","IMPRINT",EDGE,{"derivedFrom":sQuery(id+"F2.wireOp",EDGE,"E18.top")}),1.0]])]});
            var Q12;
            Q12=makeQuery(id+"F2.imprint","IMPRINT",FACE,{"disambiguationData":[TD([[makeQuery(id+"F2.imprint","IMPRINT",EDGE,{"derivedFrom":sQuery(id+"F2.wireOp",EDGE,"E96.bottom")}),-1.0]])]});
            var Q13;
            Q13=makeQuery(id+"F2.imprint","IMPRINT",FACE,{"disambiguationData":[TD([[makeQuery(id+"F2.imprint","IMPRINT",EDGE,{"derivedFrom":sQuery(id+"F2.wireOp",EDGE,"E77.bottom")}),1.0]])]});
            extrude(context, id + "F4", {"entities" : qUnion([Q0, Q1, Q2, Q3, Q4, Q5, Q6, Q7, Q8, Q9, Q10, Q11, Q12, Q13]), "operationType" : NewBodyOperationType.ADD, "depth" : 2.54 * mm, "offsetDistance" : 25.4 * mm});
        }
        {
            var Q0;
            Q0=makeQuery(id+"F2.imprint","IMPRINT",FACE,{"disambiguationData":[TD([[makeQuery(id+"F2.imprint","IMPRINT",EDGE,{"derivedFrom":sQuery(id+"F2.wireOp",EDGE,"E30.bottom")}),-1.0]])]});
            extrude(context, id + "F5", {"entities" : qUnion([Q0]), "operationType" : NewBodyOperationType.ADD, "depth" : 2.54 * mm, "offsetDistance" : 25.4 * mm});
        }
    });
